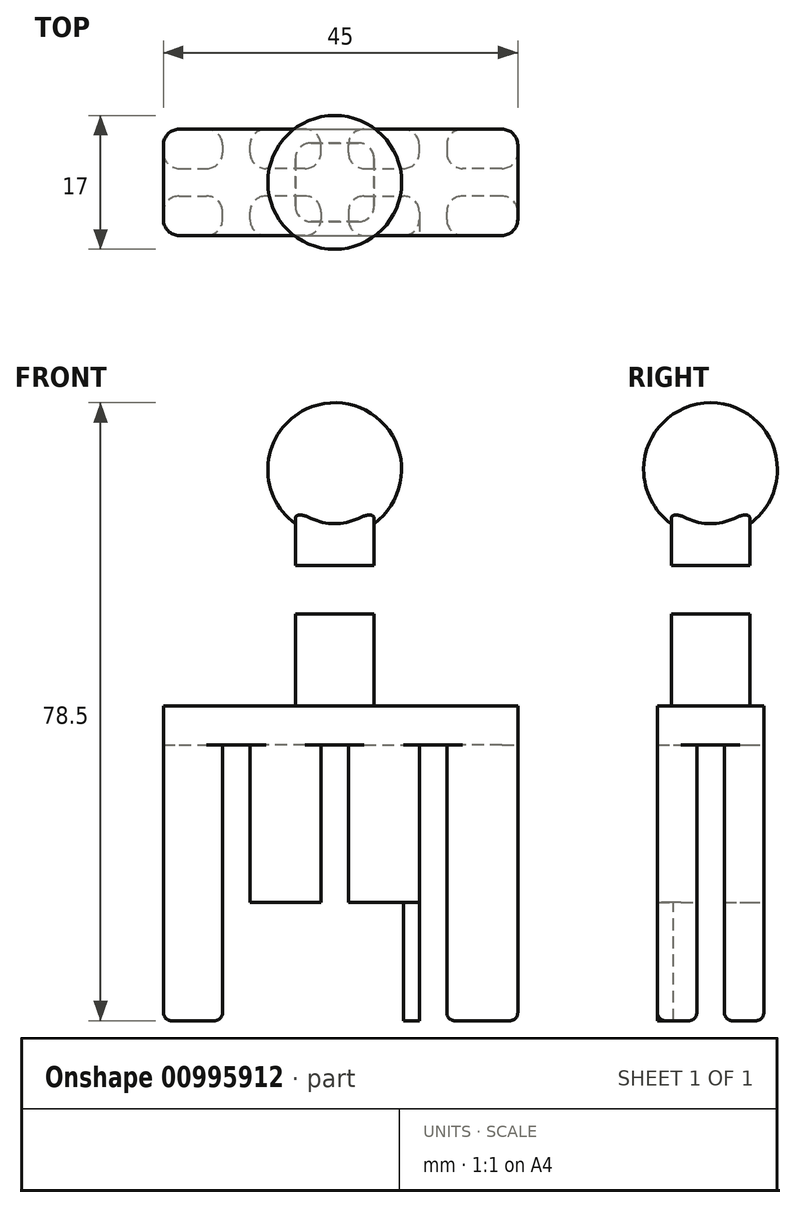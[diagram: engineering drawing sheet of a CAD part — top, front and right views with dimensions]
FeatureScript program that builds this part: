
annotation { "Feature Type Name" : "Feature", "Feature Type Description" : "" }
export const myFeature = defineFeature(function(context is Context, id is Id, definition is map)
    precondition{}
    {
        {
            var Q0;
            Q0=qCreatedBy(makeId("Top.planeOp"),FACE);
            var sketch = newSketch(context, id + "F0", { "sketchPlane" : qUnion([Q0])});
            skLineSegment(sketch, "E0.bottom", {"start": v(0, 0) * mm, "end": v(-9, 0) * mm});
            skLineSegment(sketch, "E0.top", {"start": v(0, 5) * mm, "end": v(-9, 5) * mm});
            skLineSegment(sketch, "E0.left", {"start": v(0, 0) * mm, "end": v(0, 5) * mm});
            skLineSegment(sketch, "E0.right", {"start": v(-9, 0) * mm, "end": v(-9, 5) * mm});
            skLineSegment(sketch, "E1.bottom", {"start": v(3.5, 0) * mm, "end": v(12.5, 0) * mm});
            skLineSegment(sketch, "E1.top", {"start": v(3.5, 5) * mm, "end": v(12.5, 5) * mm});
            skLineSegment(sketch, "E1.left", {"start": v(3.5, 0) * mm, "end": v(3.5, 5) * mm});
            skLineSegment(sketch, "E1.right", {"start": v(12.5, 0) * mm, "end": v(12.5, 5) * mm});
            skLineSegment(sketch, "E2.bottom", {"start": v(0, -3.5) * mm, "end": v(-9, -3.5) * mm});
            skLineSegment(sketch, "E2.top", {"start": v(0, -8.5) * mm, "end": v(-9, -8.5) * mm});
            skLineSegment(sketch, "E2.left", {"start": v(0, -3.5) * mm, "end": v(0, -8.5) * mm});
            skLineSegment(sketch, "E2.right", {"start": v(-9, -3.5) * mm, "end": v(-9, -8.5) * mm});
            skLineSegment(sketch, "E3.bottom", {"start": v(3.5, -3.5) * mm, "end": v(12.5, -3.5) * mm});
            skLineSegment(sketch, "E3.top", {"start": v(3.5, -8.5) * mm, "end": v(12.5, -8.5) * mm});
            skLineSegment(sketch, "E3.left", {"start": v(3.5, -3.5) * mm, "end": v(3.5, -8.5) * mm});
            skLineSegment(sketch, "E3.right", {"start": v(12.5, -3.5) * mm, "end": v(12.5, -8.5) * mm});
            skSolve(sketch);
        }
        {
            var Q0;
            Q0=makeQuery(id+"F0.imprint","IMPRINT",FACE,{"disambiguationData":[TD([[makeQuery(id+"F0.imprint","IMPRINT",EDGE,{"derivedFrom":sQuery(id+"F0.wireOp",EDGE,"E0.bottom")}),-1.0]])]});
            var Q1;
            Q1=makeQuery(id+"F0.imprint","IMPRINT",FACE,{"disambiguationData":[TD([[makeQuery(id+"F0.imprint","IMPRINT",EDGE,{"derivedFrom":sQuery(id+"F0.wireOp",EDGE,"E1.bottom")}),1.0]])]});
            var Q2;
            Q2=makeQuery(id+"F0.imprint","IMPRINT",FACE,{"disambiguationData":[TD([[makeQuery(id+"F0.imprint","IMPRINT",EDGE,{"derivedFrom":sQuery(id+"F0.wireOp",EDGE,"E2.bottom")}),1.0]])]});
            var Q3;
            Q3=makeQuery(id+"F0.imprint","IMPRINT",FACE,{"disambiguationData":[TD([[makeQuery(id+"F0.imprint","IMPRINT",EDGE,{"derivedFrom":sQuery(id+"F0.wireOp",EDGE,"E3.bottom")}),-1.0]])]});
            extrude(context, id + "F1", {"entities" : qUnion([Q0, Q1, Q2, Q3]), "depth" : 20 * mm, "offsetDistance" : 25 * mm});
        }
        {
            var Q0;
            Q0=makeQuery(id+"F1.opExtrude","CAP_FACE",FACE,{"disambiguationData":[OSD([sQuery(id+"F0.wireOp",EDGE,"E0.bottom"),sQuery(id+"F0.wireOp",EDGE,"E0.top"),sQuery(id+"F0.wireOp",EDGE,"E0.left"),sQuery(id+"F0.wireOp",EDGE,"E0.right")])],"isStart":false});
            var sketch = newSketch(context, id + "F2", { "sketchPlane" : qUnion([Q0])});
            skPoint(sketch, "E4.0", {"position": v(-9, 5) * mm});
            skPoint(sketch, "E5.0", {"position": v(12.5, 5) * mm});
            skPoint(sketch, "E6.0", {"position": v(12.5, -8.5) * mm});
            skPoint(sketch, "E7.0", {"position": v(-9, -8.5) * mm});
            skLineSegment(sketch, "E8.bottom", {"start": v(-9, 5) * mm, "end": v(12.5, 5) * mm});
            skLineSegment(sketch, "E8.top", {"start": v(-9, -8.5) * mm, "end": v(12.5, -8.5) * mm});
            skLineSegment(sketch, "E8.left", {"start": v(-9, 5) * mm, "end": v(-9, -8.5) * mm});
            skLineSegment(sketch, "E8.right", {"start": v(12.5, 5) * mm, "end": v(12.5, -8.5) * mm});
            skSolve(sketch);
        }
        {
            var Q0;
            {var subQ3=sQuery(id+"F2.wireOp",EDGE,"E8.top");Q0=makeQuery(id+"F2.imprint","IMPRINT",FACE,{"disambiguationData":[TD([[makeQuery(id+"F2.imprint","IMPRINT",EDGE,{"derivedFrom":subQ3}),1.0]])]});}
            var Q1;
            {var subQ4=makeQuery(id+"F1.opExtrude","CAP_EDGE",EDGE,{"disambiguationData":[OSD([sQuery(id+"F0.wireOp",EDGE,"E0.bottom")])],"isStart":false});Q1=makeQuery(id+"F2.imprint","IMPRINT",FACE,{"disambiguationData":[TD([[makeQuery(id+"F2.imprint","IMPRINT",EDGE,{"derivedFrom":subQ4}),-1.0]])]});}
            extrude(context, id + "F3", {"entities" : qUnion([Q0, Q1]), "depth" : 5 * mm, "offsetDistance" : 25 * mm});
        }
        {
            var Q0;
            Q0=makeQuery(id+"F3.opExtrude","CAP_FACE",FACE,{"disambiguationData":[OSD([sQuery(id+"F2.wireOp",EDGE,"E8.bottom"),sQuery(id+"F2.wireOp",EDGE,"E8.top"),sQuery(id+"F2.wireOp",EDGE,"E8.left"),sQuery(id+"F2.wireOp",EDGE,"E8.right")])],"isStart":false});
            var sketch = newSketch(context, id + "F4", { "sketchPlane" : qUnion([Q0])});
            skPoint(sketch, "E9.0", {"position": v(-9, 5) * mm});
            skLineSegment(sketch, "E10.0", {"start": v(12.5, 5) * mm, "end": v(12.5, -8.5) * mm});
            skPoint(sketch, "E11.0", {"position": v(-9, -8.5) * mm});
            skLineSegment(sketch, "E12.bottom", {"start": v(-3.25, 3.25) * mm, "end": v(6.75, 3.25) * mm});
            skLineSegment(sketch, "E12.top", {"start": v(-3.25, -6.75) * mm, "end": v(6.75, -6.75) * mm});
            skLineSegment(sketch, "E12.left", {"start": v(-3.25, 3.25) * mm, "end": v(-3.25, -6.75) * mm});
            skLineSegment(sketch, "E12.right", {"start": v(6.75, 3.25) * mm, "end": v(6.75, -6.75) * mm});
            skPoint(sketch, "E12.middle", {"position": v(1.75, -1.75) * mm});
            skSolve(sketch);
        }
        {
            var Q0;
            Q0=makeQuery(id+"F4.imprint","IMPRINT",FACE,{"disambiguationData":[TD([[makeQuery(id+"F4.imprint","IMPRINT",EDGE,{"derivedFrom":sQuery(id+"F4.wireOp",EDGE,"E12.bottom")}),-1.0]])]});
            extrude(context, id + "F5", {"entities" : qUnion([Q0]), "operationType" : NewBodyOperationType.ADD, "depth" : 30 * mm, "offsetDistance" : 25 * mm});
        }
        {
            var Q0;
            Q0=makeQuery(id+"F5.opExtrude","CAP_FACE",FACE,{"disambiguationData":[OSD([sQuery(id+"F4.wireOp",EDGE,"E12.bottom"),sQuery(id+"F4.wireOp",EDGE,"E12.top"),sQuery(id+"F4.wireOp",EDGE,"E12.left"),sQuery(id+"F4.wireOp",EDGE,"E12.right")])],"isStart":false});
            var sketch = newSketch(context, id + "F6", { "sketchPlane" : qUnion([Q0])});
            skLineSegment(sketch, "E13.0", {"start": v(6.75, 3.25) * mm, "end": v(6.75, -6.75) * mm, "construction": true});
            skLineSegment(sketch, "E14", {"start": v(1.75, -1.75) * mm, "end": v(1.75, 6.75) * mm});
            skPoint(sketch, "E14.endSnap0", {"position": v(1.75, 3.25) * mm});
            skLineSegment(sketch, "E15", {"start": v(1.75, -1.75) * mm, "end": v(1.75, -10.25) * mm});
            skArc(sketch, "E16", {"start": v(1.75, 6.75) * mm, "mid": v(-6.75, -1.75) * mm, "end": v(1.75, -10.25) * mm});
            skPoint(sketch, "E17.0.start.orphan", {"position": v(-3.25, 3.25) * mm});
            skPoint(sketch, "E18.end.orphan", {"position": v(-3.25, -6.75) * mm});
            skSolve(sketch);
        }
        {
            var Q0;
            {var subQ1=sQuery(id+"F6.wireOp",EDGE,"E16");Q0=makeQuery(id+"F6.imprint","IMPRINT",FACE,{"disambiguationData":[TD([[makeQuery(id+"F6.imprint","IMPRINT",EDGE,{"derivedFrom":subQ1}),1.0]])]});}
            var Q1;
            {var subQ0=makeQuery(id+"F5.opExtrude","CAP_EDGE",EDGE,{"disambiguationData":[OSD([sQuery(id+"F4.wireOp",EDGE,"E12.left")])],"isStart":false});Q1=makeQuery(id+"F6.imprint","IMPRINT",FACE,{"disambiguationData":[TD([[makeQuery(id+"F6.imprint","IMPRINT",EDGE,{"derivedFrom":subQ0}),1.0]])]});}
            var Q2;
            Q2=sQuery(id+"F6.wireOp",EDGE,"E15");
            revolve(context, id + "F7", {"operationType" : NewBodyOperationType.ADD, "surfaceOperationType" : NewSurfaceOperationType.NEW, "entities" : qUnion([Q0, Q1]), "axis" : qUnion([Q2]), "revolveType" : RevolveType.FULL});
        }
        {
            var Q0;
            Q0=makeQuery(id+"F1.opExtrude","SWEPT_BODY",BODY,{"disambiguationData":[OSD([sQuery(id+"F0.wireOp",EDGE,"E0.bottom"),sQuery(id+"F0.wireOp",EDGE,"E0.top"),sQuery(id+"F0.wireOp",EDGE,"E0.left"),sQuery(id+"F0.wireOp",EDGE,"E0.right")])]});
            var Q1;
            Q1=makeQuery(id+"F1.opExtrude","SWEPT_BODY",BODY,{"disambiguationData":[OSD([sQuery(id+"F0.wireOp",EDGE,"E1.bottom"),sQuery(id+"F0.wireOp",EDGE,"E1.top"),sQuery(id+"F0.wireOp",EDGE,"E1.left"),sQuery(id+"F0.wireOp",EDGE,"E1.right")])]});
            var Q2;
            Q2=makeQuery(id+"F1.opExtrude","SWEPT_BODY",BODY,{"disambiguationData":[OSD([sQuery(id+"F0.wireOp",EDGE,"E2.bottom"),sQuery(id+"F0.wireOp",EDGE,"E2.top"),sQuery(id+"F0.wireOp",EDGE,"E2.left"),sQuery(id+"F0.wireOp",EDGE,"E2.right")])]});
            var Q3;
            Q3=makeQuery(id+"F1.opExtrude","SWEPT_BODY",BODY,{"disambiguationData":[OSD([sQuery(id+"F0.wireOp",EDGE,"E3.bottom"),sQuery(id+"F0.wireOp",EDGE,"E3.top"),sQuery(id+"F0.wireOp",EDGE,"E3.left"),sQuery(id+"F0.wireOp",EDGE,"E3.right")])]});
            var Q4;
            Q4=makeQuery(id+"F3.opExtrude","SWEPT_BODY",BODY,{"disambiguationData":[OSD([sQuery(id+"F2.wireOp",EDGE,"E8.bottom"),sQuery(id+"F2.wireOp",EDGE,"E8.top"),sQuery(id+"F2.wireOp",EDGE,"E8.left"),sQuery(id+"F2.wireOp",EDGE,"E8.right")])]});
            booleanBodies(context, id + "F8", {"operationType" : BooleanOperationType.UNION, "tools" : qUnion([Q0, Q1, Q2, Q3, Q4])});
        }
        {
            var Q0;
            Q0=makeQuery(id+"F8.opBoolean","MERGE",EDGE,{"derivedFrom":[makeQuery(id+"F1.opExtrude","SWEPT_EDGE",EDGE,{"disambiguationData":[OSD([sQuery(id+"F0.wireOp",EDGE,"E2.top"),sQuery(id+"F0.wireOp",EDGE,"E2.right")])]}),makeQuery(id+"F3.opExtrude","SWEPT_EDGE",EDGE,{"disambiguationData":[OSD([sQuery(id+"F2.wireOp",EDGE,"E8.top"),sQuery(id+"F2.wireOp",EDGE,"E8.left")])]})]});
            var Q1;
            Q1=makeQuery(id+"F8.opBoolean","MERGE",EDGE,{"derivedFrom":[makeQuery(id+"F1.opExtrude","SWEPT_EDGE",EDGE,{"disambiguationData":[OSD([sQuery(id+"F0.wireOp",EDGE,"E3.top"),sQuery(id+"F0.wireOp",EDGE,"E3.right")])]}),makeQuery(id+"F3.opExtrude","SWEPT_EDGE",EDGE,{"disambiguationData":[OSD([sQuery(id+"F2.wireOp",EDGE,"E8.top"),sQuery(id+"F2.wireOp",EDGE,"E8.right")])]})]});
            var Q2;
            Q2=makeQuery(id+"F8.opBoolean","MERGE",EDGE,{"derivedFrom":[makeQuery(id+"F1.opExtrude","SWEPT_EDGE",EDGE,{"disambiguationData":[OSD([sQuery(id+"F0.wireOp",EDGE,"E0.top"),sQuery(id+"F0.wireOp",EDGE,"E0.right")])]}),makeQuery(id+"F3.opExtrude","SWEPT_EDGE",EDGE,{"disambiguationData":[OSD([sQuery(id+"F2.wireOp",EDGE,"E8.bottom"),sQuery(id+"F2.wireOp",EDGE,"E8.left")])]})]});
            var Q3;
            Q3=makeQuery(id+"F5.opExtrude","SWEPT_EDGE",EDGE,{"disambiguationData":[OSD([sQuery(id+"F4.wireOp",EDGE,"E12.bottom"),sQuery(id+"F4.wireOp",EDGE,"E12.left")])]});
            var Q4;
            Q4=makeQuery(id+"F5.opExtrude","SWEPT_EDGE",EDGE,{"disambiguationData":[OSD([sQuery(id+"F4.wireOp",EDGE,"E12.top"),sQuery(id+"F4.wireOp",EDGE,"E12.left")])]});
            var Q5;
            Q5=makeQuery(id+"F8.opBoolean","MERGE",EDGE,{"derivedFrom":[makeQuery(id+"F1.opExtrude","SWEPT_EDGE",EDGE,{"disambiguationData":[OSD([sQuery(id+"F0.wireOp",EDGE,"E1.top"),sQuery(id+"F0.wireOp",EDGE,"E1.right")])]}),makeQuery(id+"F3.opExtrude","SWEPT_EDGE",EDGE,{"disambiguationData":[OSD([sQuery(id+"F2.wireOp",EDGE,"E8.bottom"),sQuery(id+"F2.wireOp",EDGE,"E8.right")])]})]});
            var Q6;
            Q6=makeQuery(id+"F5.opExtrude","SWEPT_EDGE",EDGE,{"disambiguationData":[OSD([sQuery(id+"F4.wireOp",EDGE,"E12.bottom"),sQuery(id+"F4.wireOp",EDGE,"E12.right")])]});
            var Q7;
            Q7=makeQuery(id+"F5.opExtrude","SWEPT_EDGE",EDGE,{"disambiguationData":[OSD([sQuery(id+"F4.wireOp",EDGE,"E12.top"),sQuery(id+"F4.wireOp",EDGE,"E12.right")])]});
            fillet(context, id + "F9", {"entities" : qUnion([Q0, Q1, Q2, Q3, Q4, Q5, Q6, Q7]), "radius" : 2 * mm, "tangentPropagation" : true, "allowEdgeOverflow" : false});
        }
        {
            var Q0;
            Q0=makeQuery(id+"F0.imprint","IMPRINT",FACE,{"disambiguationData":[TD([[makeQuery(id+"F0.imprint","IMPRINT",EDGE,{"derivedFrom":sQuery(id+"F0.wireOp",EDGE,"E3.bottom")}),-1.0]])]});
            var sketch = newSketch(context, id + "F10", { "sketchPlane" : qUnion([Q0])});
            skArc(sketch, "E19.0", {"start": v(12.5, -6.5) * mm, "mid": v(11.91, -7.91) * mm, "end": v(10.5, -8.5) * mm});
            skLineSegment(sketch, "E20.0", {"start": v(3.5, -8.5) * mm, "end": v(10.5, -8.5) * mm});
            skLineSegment(sketch, "E21.0", {"start": v(3.5, -3.5) * mm, "end": v(3.5, -8.5) * mm});
            skLineSegment(sketch, "E22.0", {"start": v(12.5, -3.5) * mm, "end": v(12.5, -6.5) * mm});
            skLineSegment(sketch, "E23.0", {"start": v(3.5, -3.5) * mm, "end": v(12.5, -3.5) * mm});
            skLineSegment(sketch, "E24.0.0", {"start": v(-7, -8.5) * mm, "end": v(0, -8.5) * mm});
            skLineSegment(sketch, "E24.0.1", {"start": v(0, -8.5) * mm, "end": v(0, -3.5) * mm});
            skLineSegment(sketch, "E24.0.2", {"start": v(0, -3.5) * mm, "end": v(-9, -3.5) * mm});
            skLineSegment(sketch, "E24.0.3", {"start": v(-9, -3.5) * mm, "end": v(-9, -6.5) * mm});
            skArc(sketch, "E25.0", {"start": v(-7, -8.5) * mm, "mid": v(-8.41, -7.91) * mm, "end": v(-9, -6.5) * mm});
            skLineSegment(sketch, "E26.0.0", {"start": v(0, 0) * mm, "end": v(0, 5) * mm});
            skLineSegment(sketch, "E26.0.1", {"start": v(0, 5) * mm, "end": v(-7, 5) * mm});
            skLineSegment(sketch, "E26.0.2", {"start": v(-9, 3) * mm, "end": v(-9, 0) * mm});
            skLineSegment(sketch, "E26.0.3", {"start": v(-9, 0) * mm, "end": v(0, 0) * mm});
            skArc(sketch, "E27.0", {"start": v(-9, 3) * mm, "mid": v(-8.41, 4.41) * mm, "end": v(-7, 5) * mm});
            skLineSegment(sketch, "E28.0.0", {"start": v(10.5, 5) * mm, "end": v(3.5, 5) * mm});
            skLineSegment(sketch, "E28.0.1", {"start": v(3.5, 5) * mm, "end": v(3.5, 0) * mm});
            skLineSegment(sketch, "E28.0.2", {"start": v(3.5, 0) * mm, "end": v(12.5, 0) * mm});
            skLineSegment(sketch, "E28.0.3", {"start": v(12.5, 0) * mm, "end": v(12.5, 3) * mm});
            skArc(sketch, "E29.0", {"start": v(10.5, 5) * mm, "mid": v(11.91, 4.41) * mm, "end": v(12.5, 3) * mm});
            skLineSegment(sketch, "E30.top", {"start": v(0, -8.5) * mm, "end": v(-7, -8.5) * mm});
            skLineSegment(sketch, "E30.left", {"start": v(0, -3.5) * mm, "end": v(0, -8.5) * mm});
            skLineSegment(sketch, "E31.top", {"start": v(3.5, 5) * mm, "end": v(10.5, 5) * mm});
            skLineSegment(sketch, "E31.left", {"start": v(3.5, 0) * mm, "end": v(3.5, 5) * mm});
            skLineSegment(sketch, "E32.bottom", {"start": v(0, 0) * mm, "end": v(-9, 0) * mm});
            skLineSegment(sketch, "E32.right", {"start": v(-9, 0) * mm, "end": v(-9, 3) * mm});
            skPoint(sketch, "E33.orphan", {"position": v(-9, -8.5) * mm});
            skPoint(sketch, "E34.orphan", {"position": v(12.5, -8.5) * mm});
            skPoint(sketch, "E35.orphan", {"position": v(12.5, 5) * mm});
            skPoint(sketch, "E36.orphan", {"position": v(-9, 5) * mm});
            skSolve(sketch);
        }
        {
            var Q0;
            Q0=makeQuery(id+"F10.imprint","IMPRINT",FACE,{"disambiguationData":[TD([[makeQuery(id+"F10.imprint","IMPRINT",EDGE,{"derivedFrom":sQuery(id+"F10.wireOp",EDGE,"E19.0")}),-1.0]])]});
            var Q1;
            Q1=makeQuery(id+"F10.imprint","IMPRINT",FACE,{"disambiguationData":[TD([[makeQuery(id+"F10.imprint","IMPRINT",EDGE,{"derivedFrom":sQuery(id+"F10.wireOp",EDGE,"E25.0")}),-1.0]])]});
            var Q2;
            Q2=makeQuery(id+"F10.imprint","IMPRINT",FACE,{"disambiguationData":[TD([[makeQuery(id+"F10.imprint","IMPRINT",EDGE,{"derivedFrom":sQuery(id+"F10.wireOp",EDGE,"E29.0")}),-1.0]])]});
            var Q3;
            Q3=makeQuery(id+"F10.imprint","IMPRINT",FACE,{"disambiguationData":[TD([[makeQuery(id+"F10.imprint","IMPRINT",EDGE,{"derivedFrom":sQuery(id+"F10.wireOp",EDGE,"E27.0")}),-1.0]])]});
            extrude(context, id + "F11", {"entities" : qUnion([Q0, Q1, Q2, Q3]), "operationType" : NewBodyOperationType.ADD, "oppositeDirection" : true, "depth" : 15 * mm, "offsetDistance" : 25 * mm});
        }
        {
            var Q0;
            Q0=makeQuery(id+"F5.opExtrude","SWEPT_FACE",FACE,{"disambiguationData":[OSD([sQuery(id+"F4.wireOp",EDGE,"E12.top")])]});
            var sketch = newSketch(context, id + "F12", { "sketchPlane" : qUnion([Q0])});
            skLineSegment(sketch, "E37.bottom", {"start": v(11.4, 42.86) * mm, "end": v(-9.18, 42.86) * mm});
            skLineSegment(sketch, "E37.top", {"start": v(11.4, 36.69) * mm, "end": v(-9.18, 36.69) * mm});
            skLineSegment(sketch, "E37.left", {"start": v(11.4, 42.86) * mm, "end": v(11.4, 36.69) * mm});
            skLineSegment(sketch, "E37.right", {"start": v(-9.18, 42.86) * mm, "end": v(-9.18, 36.69) * mm});
            skSolve(sketch);
        }
        {
            var Q0;
            {var subQ0=sQuery(id+"F12.wireOp",EDGE,"E37.left");Q0=makeQuery(id+"F12.imprint","IMPRINT",FACE,{"disambiguationData":[TD([[makeQuery(id+"F12.imprint","IMPRINT",EDGE,{"derivedFrom":subQ0}),-1.0]])]});}
            var Q1;
            {var subQ0=sQuery(id+"F12.wireOp",EDGE,"E37.bottom");var subQ1=sQuery(id+"F4.wireOp",EDGE,"E12.top");var subQ2=makeQuery(id+"F5.opExtrude","SWEPT_FACE",FACE,{"disambiguationData":[OSD([subQ1])]});var subQ3=makeQuery(id+"F9.opFillet","BLEND_EDGE",EDGE,{"blendedFrom":[makeQuery(id+"F5.opExtrude","SWEPT_EDGE",EDGE,{"disambiguationData":[OSD([subQ1,sQuery(id+"F4.wireOp",EDGE,"E12.right")])]}),subQ2],"blendedInto":[subQ2]});var subQ4=makeQuery(id+"F12.imprint","INTERSECT",VERTEX,{"derivedFrom":[subQ3,subQ0]});Q1=makeQuery(id+"F12.imprint","IMPRINT",FACE,{"disambiguationData":[TD([[makeQuery(id+"F12.imprint","IMPRINT",EDGE,{"disambiguationData":[TD([[subQ4,-1.0]])],"derivedFrom":subQ0}),1.0]])]});}
            var Q2;
            {var subQ0=sQuery(id+"F12.wireOp",EDGE,"E37.right");Q2=makeQuery(id+"F12.imprint","IMPRINT",FACE,{"disambiguationData":[TD([[makeQuery(id+"F12.imprint","IMPRINT",EDGE,{"derivedFrom":subQ0}),1.0]])]});}
            extrude(context, id + "F13", {"entities" : qUnion([Q0, Q1, Q2]), "operationType" : NewBodyOperationType.REMOVE, "oppositeDirection" : true, "depth" : 25 * mm, "offsetDistance" : 25 * mm});
        }
        {
            var Q0;
            Q0=makeQuery(id+"F11.boolean.opBoolean","MERGE",FACE,{"derivedFrom":[makeQuery(id+"F8.opBoolean","MERGE",FACE,{"derivedFrom":[makeQuery(id+"F1.opExtrude","SWEPT_FACE",FACE,{"disambiguationData":[OSD([sQuery(id+"F0.wireOp",EDGE,"E1.right")])]}),makeQuery(id+"F1.opExtrude","SWEPT_FACE",FACE,{"disambiguationData":[OSD([sQuery(id+"F0.wireOp",EDGE,"E3.right")])]}),makeQuery(id+"F3.opExtrude","SWEPT_FACE",FACE,{"disambiguationData":[OSD([sQuery(id+"F2.wireOp",EDGE,"E8.right")])]})]}),makeQuery(id+"F11.opExtrude","SWEPT_FACE",FACE,{"disambiguationData":[OSD([sQuery(id+"F10.wireOp",EDGE,"E22.0")])]}),makeQuery(id+"F11.opExtrude","SWEPT_FACE",FACE,{"disambiguationData":[OSD([sQuery(id+"F10.wireOp",EDGE,"E28.0.3")])]})]});
            var sketch = newSketch(context, id + "F14", { "sketchPlane" : qUnion([Q0])});
            skPoint(sketch, "E38.0", {"position": v(5, 25) * mm});
            skPoint(sketch, "E39.0", {"position": v(-8.5, 25) * mm});
            skPoint(sketch, "E40.0", {"position": v(0, 20) * mm});
            skPoint(sketch, "E41.0", {"position": v(-3.5, 20) * mm});
            skLineSegment(sketch, "E42.bottom", {"start": v(5, 25) * mm, "end": v(0, 25) * mm});
            skLineSegment(sketch, "E42.top", {"start": v(5, 20) * mm, "end": v(0, 20) * mm});
            skLineSegment(sketch, "E42.left", {"start": v(5, 25) * mm, "end": v(5, 20) * mm});
            skLineSegment(sketch, "E42.right", {"start": v(0, 25) * mm, "end": v(0, 20) * mm});
            skLineSegment(sketch, "E43.bottom", {"start": v(-8.5, 25) * mm, "end": v(-3.5, 25) * mm});
            skLineSegment(sketch, "E43.top", {"start": v(-8.5, 20) * mm, "end": v(-3.5, 20) * mm});
            skLineSegment(sketch, "E43.left", {"start": v(-8.5, 25) * mm, "end": v(-8.5, 20) * mm});
            skLineSegment(sketch, "E43.right", {"start": v(-3.5, 25) * mm, "end": v(-3.5, 20) * mm});
            skLineSegment(sketch, "E44.bottom", {"start": v(-3.5, 25) * mm, "end": v(0, 25) * mm});
            skLineSegment(sketch, "E44.top", {"start": v(-3.5, 20) * mm, "end": v(0, 20) * mm});
            skSolve(sketch);
        }
        {
            var Q0;
            {var subQ6=sQuery(id+"F14.wireOp",EDGE,"E43.right");Q0=makeQuery(id+"F14.imprint","IMPRINT",FACE,{"disambiguationData":[TD([[makeQuery(id+"F14.imprint","IMPRINT",EDGE,{"derivedFrom":subQ6}),-1.0]])]});}
            var Q1;
            {var subQ5=sQuery(id+"F14.wireOp",EDGE,"E43.left");Q1=makeQuery(id+"F14.imprint","IMPRINT",FACE,{"disambiguationData":[TD([[makeQuery(id+"F14.imprint","IMPRINT",EDGE,{"derivedFrom":subQ5}),1.0]])]});}
            var Q2;
            {var subQ6=sQuery(id+"F14.wireOp",EDGE,"E42.right");Q2=makeQuery(id+"F14.imprint","IMPRINT",FACE,{"disambiguationData":[TD([[makeQuery(id+"F14.imprint","IMPRINT",EDGE,{"derivedFrom":subQ6}),1.0]])]});}
            var Q3;
            Q3=makeQuery(id+"F14.imprint","IMPRINT",FACE,{"disambiguationData":[TD([[makeQuery(id+"F14.imprint","IMPRINT",EDGE,{"derivedFrom":sQuery(id+"F14.wireOp",EDGE,"E44.bottom")}),1.0]])]});
            var Q4;
            {var subQ5=sQuery(id+"F14.wireOp",EDGE,"E42.left");Q4=makeQuery(id+"F14.imprint","IMPRINT",FACE,{"disambiguationData":[TD([[makeQuery(id+"F14.imprint","IMPRINT",EDGE,{"derivedFrom":subQ5}),-1.0]])]});}
            extrude(context, id + "F15", {"entities" : qUnion([Q0, Q1, Q2, Q3, Q4]), "operationType" : NewBodyOperationType.ADD, "depth" : 12.5 * mm, "offsetDistance" : 25 * mm, "hasSecondDirection" : true, "secondDirectionOppositeDirection" : true, "secondDirectionDepth" : 32.5 * mm});
        }
        {
            var Q0;
            Q0=makeQuery(id+"F15.boolean.opBoolean","MERGE",FACE,{"derivedFrom":[makeQuery(id+"F3.opExtrude","CAP_FACE",FACE,{"disambiguationData":[OSD([sQuery(id+"F2.wireOp",EDGE,"E8.bottom"),sQuery(id+"F2.wireOp",EDGE,"E8.top"),sQuery(id+"F2.wireOp",EDGE,"E8.left"),sQuery(id+"F2.wireOp",EDGE,"E8.right")])],"isStart":true}),makeQuery(id+"F15.opExtrude","SWEPT_FACE",FACE,{"disambiguationData":[OSD([sQuery(id+"F14.wireOp",EDGE,"E42.top"),sQuery(id+"F14.wireOp",EDGE,"E43.top"),sQuery(id+"F14.wireOp",EDGE,"E44.top")])]})]});
            var sketch = newSketch(context, id + "F16", { "sketchPlane" : qUnion([Q0])});
            skLineSegment(sketch, "E45.bottom", {"start": v(25, 8.5) * mm, "end": v(16, 8.5) * mm});
            skLineSegment(sketch, "E45.top", {"start": v(25, 3.5) * mm, "end": v(16, 3.5) * mm});
            skLineSegment(sketch, "E45.left", {"start": v(25, 8.5) * mm, "end": v(25, 3.5) * mm});
            skLineSegment(sketch, "E45.right", {"start": v(16, 8.5) * mm, "end": v(16, 3.5) * mm});
            skLineSegment(sketch, "E46.bottom", {"start": v(25, -5) * mm, "end": v(16, -5) * mm});
            skLineSegment(sketch, "E46.top", {"start": v(25, 0) * mm, "end": v(16, 0) * mm});
            skLineSegment(sketch, "E46.left", {"start": v(25, -5) * mm, "end": v(25, 0) * mm});
            skLineSegment(sketch, "E46.right", {"start": v(16, -5) * mm, "end": v(16, 0) * mm});
            skLineSegment(sketch, "E47.bottom", {"start": v(-20, 8.5) * mm, "end": v(-12.5, 8.5) * mm});
            skLineSegment(sketch, "E47.top", {"start": v(-20, 3.5) * mm, "end": v(-12.5, 3.5) * mm});
            skLineSegment(sketch, "E47.left", {"start": v(-20, 8.5) * mm, "end": v(-20, 3.5) * mm});
            skLineSegment(sketch, "E47.right", {"start": v(-12.5, 8.5) * mm, "end": v(-12.5, 3.5) * mm});
            skLineSegment(sketch, "E48.bottom", {"start": v(-20, -5) * mm, "end": v(-12.5, -5) * mm});
            skLineSegment(sketch, "E48.top", {"start": v(-20, 0) * mm, "end": v(-12.5, 0) * mm});
            skLineSegment(sketch, "E48.left", {"start": v(-20, -5) * mm, "end": v(-20, 0) * mm});
            skLineSegment(sketch, "E48.right", {"start": v(-12.5, -5) * mm, "end": v(-12.5, 0) * mm});
            skSolve(sketch);
        }
        {
            var Q0;
            Q0=makeQuery(id+"F16.imprint","IMPRINT",FACE,{"disambiguationData":[TD([[makeQuery(id+"F16.imprint","IMPRINT",EDGE,{"derivedFrom":sQuery(id+"F16.wireOp",EDGE,"E45.bottom")}),1.0]])]});
            var Q1;
            Q1=makeQuery(id+"F16.imprint","IMPRINT",FACE,{"disambiguationData":[TD([[makeQuery(id+"F16.imprint","IMPRINT",EDGE,{"derivedFrom":sQuery(id+"F16.wireOp",EDGE,"E46.bottom")}),-1.0]])]});
            var Q2;
            Q2=makeQuery(id+"F16.imprint","IMPRINT",FACE,{"disambiguationData":[TD([[makeQuery(id+"F16.imprint","IMPRINT",EDGE,{"derivedFrom":sQuery(id+"F16.wireOp",EDGE,"E48.bottom")}),-1.0]])]});
            var Q3;
            Q3=makeQuery(id+"F16.imprint","IMPRINT",FACE,{"disambiguationData":[TD([[makeQuery(id+"F16.imprint","IMPRINT",EDGE,{"derivedFrom":sQuery(id+"F16.wireOp",EDGE,"E47.bottom")}),1.0]])]});
            extrude(context, id + "F17", {"entities" : qUnion([Q0, Q1, Q2, Q3]), "operationType" : NewBodyOperationType.ADD, "depth" : 35 * mm, "offsetDistance" : 25 * mm});
        }
        {
            var Q0;
            Q0=makeQuery(id+"F17.boolean.opBoolean","MERGE",EDGE,{"derivedFrom":[makeQuery(id+"F15.opExtrude","CAP_EDGE",EDGE,{"disambiguationData":[OSD([sQuery(id+"F14.wireOp",EDGE,"E42.left")])],"isStart":false}),makeQuery(id+"F17.opExtrude","SWEPT_EDGE",EDGE,{"disambiguationData":[OSD([sQuery(id+"F16.wireOp",EDGE,"E46.bottom"),sQuery(id+"F16.wireOp",EDGE,"E46.left")])]})]});
            var Q1;
            Q1=makeQuery(id+"F17.opExtrude","SWEPT_EDGE",EDGE,{"disambiguationData":[OSD([sQuery(id+"F14.wireOp",EDGE,"E42.top"),sQuery(id+"F14.wireOp",EDGE,"E42.left"),sQuery(id+"F16.wireOp",EDGE,"E46.bottom"),sQuery(id+"F16.wireOp",EDGE,"E46.right")])]});
            var Q2;
            Q2=makeQuery(id+"F11.boolean.opBoolean","MERGE",EDGE,{"derivedFrom":[makeQuery(id+"F1.opExtrude","SWEPT_EDGE",EDGE,{"disambiguationData":[OSD([sQuery(id+"F0.wireOp",EDGE,"E1.top"),sQuery(id+"F0.wireOp",EDGE,"E1.left")])]}),makeQuery(id+"F11.opExtrude","SWEPT_EDGE",EDGE,{"disambiguationData":[OSD([sQuery(id+"F10.wireOp",EDGE,"E31.top"),sQuery(id+"F10.wireOp",EDGE,"E31.left")])]})]});
            var Q3;
            Q3=makeQuery(id+"F11.boolean.opBoolean","MERGE",EDGE,{"derivedFrom":[makeQuery(id+"F1.opExtrude","SWEPT_EDGE",EDGE,{"disambiguationData":[OSD([sQuery(id+"F0.wireOp",EDGE,"E0.top"),sQuery(id+"F0.wireOp",EDGE,"E0.left")])]}),makeQuery(id+"F11.opExtrude","SWEPT_EDGE",EDGE,{"disambiguationData":[OSD([sQuery(id+"F10.wireOp",EDGE,"E26.0.1"),sQuery(id+"F10.wireOp",EDGE,"E26.0.0")])]})]});
            var Q4;
            Q4=makeQuery(id+"F17.opExtrude","SWEPT_EDGE",EDGE,{"disambiguationData":[OSD([sQuery(id+"F14.wireOp",EDGE,"E42.top"),sQuery(id+"F14.wireOp",EDGE,"E42.left"),sQuery(id+"F16.wireOp",EDGE,"E48.bottom"),sQuery(id+"F16.wireOp",EDGE,"E48.right")])]});
            var Q5;
            Q5=makeQuery(id+"F17.boolean.opBoolean","MERGE",EDGE,{"derivedFrom":[makeQuery(id+"F15.opExtrude","CAP_EDGE",EDGE,{"disambiguationData":[OSD([sQuery(id+"F14.wireOp",EDGE,"E42.left")])],"isStart":true}),makeQuery(id+"F17.opExtrude","SWEPT_EDGE",EDGE,{"disambiguationData":[OSD([sQuery(id+"F16.wireOp",EDGE,"E48.bottom"),sQuery(id+"F16.wireOp",EDGE,"E48.left")])]})]});
            var Q6;
            Q6=makeQuery(id+"F17.boolean.opBoolean","MERGE",EDGE,{"derivedFrom":[makeQuery(id+"F15.opExtrude","CAP_EDGE",EDGE,{"disambiguationData":[OSD([sQuery(id+"F14.wireOp",EDGE,"E43.left")])],"isStart":true}),makeQuery(id+"F17.opExtrude","SWEPT_EDGE",EDGE,{"disambiguationData":[OSD([sQuery(id+"F16.wireOp",EDGE,"E47.bottom"),sQuery(id+"F16.wireOp",EDGE,"E47.left")])]})]});
            var Q7;
            Q7=makeQuery(id+"F17.opExtrude","SWEPT_EDGE",EDGE,{"disambiguationData":[OSD([sQuery(id+"F14.wireOp",EDGE,"E43.top"),sQuery(id+"F14.wireOp",EDGE,"E43.left"),sQuery(id+"F16.wireOp",EDGE,"E47.bottom"),sQuery(id+"F16.wireOp",EDGE,"E47.right")])]});
            var Q8;
            Q8=makeQuery(id+"F11.boolean.opBoolean","MERGE",EDGE,{"derivedFrom":[makeQuery(id+"F1.opExtrude","SWEPT_EDGE",EDGE,{"disambiguationData":[OSD([sQuery(id+"F0.wireOp",EDGE,"E2.top"),sQuery(id+"F0.wireOp",EDGE,"E2.left")])]}),makeQuery(id+"F11.opExtrude","SWEPT_EDGE",EDGE,{"disambiguationData":[OSD([sQuery(id+"F10.wireOp",EDGE,"E30.top"),sQuery(id+"F10.wireOp",EDGE,"E30.left")])]})]});
            var Q9;
            Q9=makeQuery(id+"F11.boolean.opBoolean","MERGE",EDGE,{"derivedFrom":[makeQuery(id+"F1.opExtrude","SWEPT_EDGE",EDGE,{"disambiguationData":[OSD([sQuery(id+"F0.wireOp",EDGE,"E3.top"),sQuery(id+"F0.wireOp",EDGE,"E3.left")])]}),makeQuery(id+"F11.opExtrude","SWEPT_EDGE",EDGE,{"disambiguationData":[OSD([sQuery(id+"F10.wireOp",EDGE,"E20.0"),sQuery(id+"F10.wireOp",EDGE,"E21.0")])]})]});
            var Q10;
            Q10=makeQuery(id+"F17.boolean.opBoolean","MERGE",EDGE,{"derivedFrom":[makeQuery(id+"F15.opExtrude","CAP_EDGE",EDGE,{"disambiguationData":[OSD([sQuery(id+"F14.wireOp",EDGE,"E43.left")])],"isStart":false}),makeQuery(id+"F17.opExtrude","SWEPT_EDGE",EDGE,{"disambiguationData":[OSD([sQuery(id+"F16.wireOp",EDGE,"E45.bottom"),sQuery(id+"F16.wireOp",EDGE,"E45.left")])]})]});
            var Q11;
            Q11=makeQuery(id+"F17.opExtrude","SWEPT_EDGE",EDGE,{"disambiguationData":[OSD([sQuery(id+"F14.wireOp",EDGE,"E43.top"),sQuery(id+"F14.wireOp",EDGE,"E43.left"),sQuery(id+"F16.wireOp",EDGE,"E45.bottom"),sQuery(id+"F16.wireOp",EDGE,"E45.right")])]});
            var Q12;
            Q12=makeQuery(id+"F17.opExtrude","SWEPT_EDGE",EDGE,{"disambiguationData":[OSD([sQuery(id+"F14.wireOp",EDGE,"E42.top"),sQuery(id+"F14.wireOp",EDGE,"E43.top"),sQuery(id+"F14.wireOp",EDGE,"E44.top"),sQuery(id+"F16.wireOp",EDGE,"E48.top"),sQuery(id+"F16.wireOp",EDGE,"E48.left")])]});
            var Q13;
            Q13=makeQuery(id+"F17.opExtrude","SWEPT_EDGE",EDGE,{"disambiguationData":[OSD([sQuery(id+"F14.wireOp",EDGE,"E42.top"),sQuery(id+"F14.wireOp",EDGE,"E43.top"),sQuery(id+"F14.wireOp",EDGE,"E44.top"),sQuery(id+"F16.wireOp",EDGE,"E47.top"),sQuery(id+"F16.wireOp",EDGE,"E47.left")])]});
            var Q14;
            Q14=makeQuery(id+"F17.opExtrude","SWEPT_EDGE",EDGE,{"disambiguationData":[OSD([sQuery(id+"F16.wireOp",EDGE,"E48.top"),sQuery(id+"F16.wireOp",EDGE,"E48.right")])]});
            var Q15;
            Q15=makeQuery(id+"F17.opExtrude","SWEPT_EDGE",EDGE,{"disambiguationData":[OSD([sQuery(id+"F16.wireOp",EDGE,"E47.top"),sQuery(id+"F16.wireOp",EDGE,"E47.right")])]});
            var Q16;
            Q16=makeQuery(id+"F11.boolean.opBoolean","MERGE",EDGE,{"derivedFrom":[makeQuery(id+"F1.opExtrude","SWEPT_EDGE",EDGE,{"disambiguationData":[OSD([sQuery(id+"F0.wireOp",EDGE,"E0.bottom"),sQuery(id+"F0.wireOp",EDGE,"E0.right")])]}),makeQuery(id+"F11.opExtrude","SWEPT_EDGE",EDGE,{"disambiguationData":[OSD([sQuery(id+"F10.wireOp",EDGE,"E32.bottom"),sQuery(id+"F10.wireOp",EDGE,"E32.right")])]})]});
            var Q17;
            Q17=makeQuery(id+"F11.boolean.opBoolean","MERGE",EDGE,{"derivedFrom":[makeQuery(id+"F1.opExtrude","SWEPT_EDGE",EDGE,{"disambiguationData":[OSD([sQuery(id+"F0.wireOp",EDGE,"E2.bottom"),sQuery(id+"F0.wireOp",EDGE,"E2.right")])]}),makeQuery(id+"F11.opExtrude","SWEPT_EDGE",EDGE,{"disambiguationData":[OSD([sQuery(id+"F10.wireOp",EDGE,"E24.0.2"),sQuery(id+"F10.wireOp",EDGE,"E24.0.3")])]})]});
            var Q18;
            Q18=makeQuery(id+"F11.boolean.opBoolean","MERGE",EDGE,{"derivedFrom":[makeQuery(id+"F1.opExtrude","SWEPT_EDGE",EDGE,{"disambiguationData":[OSD([sQuery(id+"F0.wireOp",EDGE,"E3.bottom"),sQuery(id+"F0.wireOp",EDGE,"E3.left")])]}),makeQuery(id+"F11.opExtrude","SWEPT_EDGE",EDGE,{"disambiguationData":[OSD([sQuery(id+"F10.wireOp",EDGE,"E23.0"),sQuery(id+"F10.wireOp",EDGE,"E21.0")])]})]});
            var Q19;
            Q19=makeQuery(id+"F11.boolean.opBoolean","MERGE",EDGE,{"derivedFrom":[makeQuery(id+"F1.opExtrude","SWEPT_EDGE",EDGE,{"disambiguationData":[OSD([sQuery(id+"F0.wireOp",EDGE,"E1.bottom"),sQuery(id+"F0.wireOp",EDGE,"E1.left")])]}),makeQuery(id+"F11.opExtrude","SWEPT_EDGE",EDGE,{"disambiguationData":[OSD([sQuery(id+"F10.wireOp",EDGE,"E28.0.2"),sQuery(id+"F10.wireOp",EDGE,"E31.left")])]})]});
            var Q20;
            Q20=makeQuery(id+"F11.boolean.opBoolean","MERGE",EDGE,{"derivedFrom":[makeQuery(id+"F1.opExtrude","SWEPT_EDGE",EDGE,{"disambiguationData":[OSD([sQuery(id+"F0.wireOp",EDGE,"E0.bottom"),sQuery(id+"F0.wireOp",EDGE,"E0.left")])]}),makeQuery(id+"F11.opExtrude","SWEPT_EDGE",EDGE,{"disambiguationData":[OSD([sQuery(id+"F10.wireOp",EDGE,"E32.bottom"),sQuery(id+"F10.wireOp",EDGE,"E26.0.0")])]})]});
            var Q21;
            Q21=makeQuery(id+"F11.boolean.opBoolean","MERGE",EDGE,{"derivedFrom":[makeQuery(id+"F1.opExtrude","SWEPT_EDGE",EDGE,{"disambiguationData":[OSD([sQuery(id+"F0.wireOp",EDGE,"E2.bottom"),sQuery(id+"F0.wireOp",EDGE,"E2.left")])]}),makeQuery(id+"F11.opExtrude","SWEPT_EDGE",EDGE,{"disambiguationData":[OSD([sQuery(id+"F10.wireOp",EDGE,"E24.0.2"),sQuery(id+"F10.wireOp",EDGE,"E30.left")])]})]});
            var Q22;
            Q22=makeQuery(id+"F11.boolean.opBoolean","MERGE",EDGE,{"derivedFrom":[makeQuery(id+"F1.opExtrude","SWEPT_EDGE",EDGE,{"disambiguationData":[OSD([sQuery(id+"F0.wireOp",EDGE,"E1.bottom"),sQuery(id+"F0.wireOp",EDGE,"E1.right")])]}),makeQuery(id+"F11.opExtrude","SWEPT_EDGE",EDGE,{"disambiguationData":[OSD([sQuery(id+"F10.wireOp",EDGE,"E28.0.2"),sQuery(id+"F10.wireOp",EDGE,"E28.0.3")])]})]});
            var Q23;
            Q23=makeQuery(id+"F11.boolean.opBoolean","MERGE",EDGE,{"derivedFrom":[makeQuery(id+"F1.opExtrude","SWEPT_EDGE",EDGE,{"disambiguationData":[OSD([sQuery(id+"F0.wireOp",EDGE,"E3.bottom"),sQuery(id+"F0.wireOp",EDGE,"E3.right")])]}),makeQuery(id+"F11.opExtrude","SWEPT_EDGE",EDGE,{"disambiguationData":[OSD([sQuery(id+"F10.wireOp",EDGE,"E23.0"),sQuery(id+"F10.wireOp",EDGE,"E22.0")])]})]});
            var Q24;
            Q24=makeQuery(id+"F17.opExtrude","SWEPT_EDGE",EDGE,{"disambiguationData":[OSD([sQuery(id+"F16.wireOp",EDGE,"E46.top"),sQuery(id+"F16.wireOp",EDGE,"E46.right")])]});
            var Q25;
            Q25=makeQuery(id+"F17.opExtrude","SWEPT_EDGE",EDGE,{"disambiguationData":[OSD([sQuery(id+"F16.wireOp",EDGE,"E45.top"),sQuery(id+"F16.wireOp",EDGE,"E45.right")])]});
            var Q26;
            Q26=makeQuery(id+"F17.opExtrude","SWEPT_EDGE",EDGE,{"disambiguationData":[OSD([sQuery(id+"F14.wireOp",EDGE,"E42.top"),sQuery(id+"F14.wireOp",EDGE,"E43.top"),sQuery(id+"F14.wireOp",EDGE,"E44.top"),sQuery(id+"F16.wireOp",EDGE,"E45.top"),sQuery(id+"F16.wireOp",EDGE,"E45.left")])]});
            var Q27;
            Q27=makeQuery(id+"F17.opExtrude","SWEPT_EDGE",EDGE,{"disambiguationData":[OSD([sQuery(id+"F14.wireOp",EDGE,"E42.top"),sQuery(id+"F14.wireOp",EDGE,"E43.top"),sQuery(id+"F14.wireOp",EDGE,"E44.top"),sQuery(id+"F16.wireOp",EDGE,"E46.top"),sQuery(id+"F16.wireOp",EDGE,"E46.left")])]});
            fillet(context, id + "F18", {"entities" : qUnion([Q0, Q1, Q2, Q3, Q4, Q5, Q6, Q7, Q8, Q9, Q10, Q11, Q12, Q13, Q14, Q15, Q16, Q17, Q18, Q19, Q20, Q21, Q22, Q23, Q24, Q25, Q26, Q27]), "radius" : 2 * mm, "tangentPropagation" : true, "allowEdgeOverflow" : false});
        }
        {
            var Q0;
            Q0=makeQuery(id+"F17.opExtrude","CAP_FACE",FACE,{"disambiguationData":[OSD([sQuery(id+"F16.wireOp",EDGE,"E48.bottom"),sQuery(id+"F16.wireOp",EDGE,"E48.top"),sQuery(id+"F16.wireOp",EDGE,"E48.left"),sQuery(id+"F16.wireOp",EDGE,"E48.right")])],"isStart":false});
            var Q1;
            Q1=makeQuery(id+"F17.opExtrude","CAP_FACE",FACE,{"disambiguationData":[OSD([sQuery(id+"F16.wireOp",EDGE,"E46.bottom"),sQuery(id+"F16.wireOp",EDGE,"E46.top"),sQuery(id+"F16.wireOp",EDGE,"E46.left"),sQuery(id+"F16.wireOp",EDGE,"E46.right")])],"isStart":false});
            var Q2;
            Q2=makeQuery(id+"F17.opExtrude","CAP_FACE",FACE,{"disambiguationData":[OSD([sQuery(id+"F16.wireOp",EDGE,"E45.bottom"),sQuery(id+"F16.wireOp",EDGE,"E45.top"),sQuery(id+"F16.wireOp",EDGE,"E45.left"),sQuery(id+"F16.wireOp",EDGE,"E45.right")])],"isStart":false});
            var Q3;
            Q3=makeQuery(id+"F11.opExtrude","CAP_FACE",FACE,{"disambiguationData":[OSD([sQuery(id+"F10.wireOp",EDGE,"E19.0"),sQuery(id+"F10.wireOp",EDGE,"E23.0"),sQuery(id+"F10.wireOp",EDGE,"E20.0"),sQuery(id+"F10.wireOp",EDGE,"E21.0"),sQuery(id+"F10.wireOp",EDGE,"E22.0")])],"isStart":false});
            var Q4;
            Q4=makeQuery(id+"F11.opExtrude","CAP_FACE",FACE,{"disambiguationData":[OSD([sQuery(id+"F10.wireOp",EDGE,"E25.0"),sQuery(id+"F10.wireOp",EDGE,"E24.0.2"),sQuery(id+"F10.wireOp",EDGE,"E30.top"),sQuery(id+"F10.wireOp",EDGE,"E30.left"),sQuery(id+"F10.wireOp",EDGE,"E24.0.3")])],"isStart":false});
            var Q5;
            Q5=makeQuery(id+"F17.opExtrude","CAP_FACE",FACE,{"disambiguationData":[OSD([sQuery(id+"F16.wireOp",EDGE,"E47.bottom"),sQuery(id+"F16.wireOp",EDGE,"E47.top"),sQuery(id+"F16.wireOp",EDGE,"E47.left"),sQuery(id+"F16.wireOp",EDGE,"E47.right")])],"isStart":false});
            var Q6;
            Q6=makeQuery(id+"F11.opExtrude","CAP_FACE",FACE,{"disambiguationData":[OSD([sQuery(id+"F10.wireOp",EDGE,"E27.0"),sQuery(id+"F10.wireOp",EDGE,"E32.bottom"),sQuery(id+"F10.wireOp",EDGE,"E26.0.1"),sQuery(id+"F10.wireOp",EDGE,"E26.0.0"),sQuery(id+"F10.wireOp",EDGE,"E32.right")])],"isStart":false});
            var Q7;
            Q7=makeQuery(id+"F11.opExtrude","CAP_FACE",FACE,{"disambiguationData":[OSD([sQuery(id+"F10.wireOp",EDGE,"E29.0"),sQuery(id+"F10.wireOp",EDGE,"E28.0.2"),sQuery(id+"F10.wireOp",EDGE,"E31.top"),sQuery(id+"F10.wireOp",EDGE,"E31.left"),sQuery(id+"F10.wireOp",EDGE,"E28.0.3")])],"isStart":false});
            fillet(context, id + "F19", {"entities" : qUnion([Q0, Q1, Q2, Q3, Q4, Q5, Q6, Q7]), "radius" : 1 * mm, "tangentPropagation" : true, "allowEdgeOverflow" : false});
        }
    });
